# Revit family: Furniture-Counter_Top-KOHLER-Quartz-K-36573-1
name_source: partatom
category: Specialty Equipment
units: mm (PartAtom-declared; Revit-internal decimal feet)

## family parameters
Cut with Voids When Loaded = No
Host = Face
OmniClass Number = 23.21.19.15
OmniClass Title = Specialty Casework
Part Type = Normal
Room Calculation Point = No
Round Connector Dimension = Use Diameter
Shared = No

## types (2) — shared parameters
ADA Compliant = No
Assembly Code = C1030200
Date Modified = 07/17/2024
Default Elevation = 42"
Description = 73 Top With 2 Rectangular Undermount Cutout NS
Height = 1 3/16"
Length = 73 1/8"
Manufacturer = Kohler Co.
Master Format 2014 = 10 28 00
Master Format 2014 Name = Toilet, Bath, and Laundry Accessories
Material = Quartz
Product Documentation Link = https://www.us.kohler.com
Product Name = Quartz
Product Page URL = http://www.us.kohler.com
URL = https://www.us.kohler.com
WaterSense Certified = No
Width = 22 7/16"

## per-type parameters (varying)
| type | Finish | Model | Type |
| EST-Eternal Statuario | KOHLER-Quartz-EST-Eternal_Statuario | K-36573-EST | 1 |
| MMW-Miami White | KOHLER-Quartz-MMW-Miami_White | K-36573-MMW | 2 |

## geometry (parser evidence)
native form markers: Sweep x4
no freeform markers — native parametric forms only
